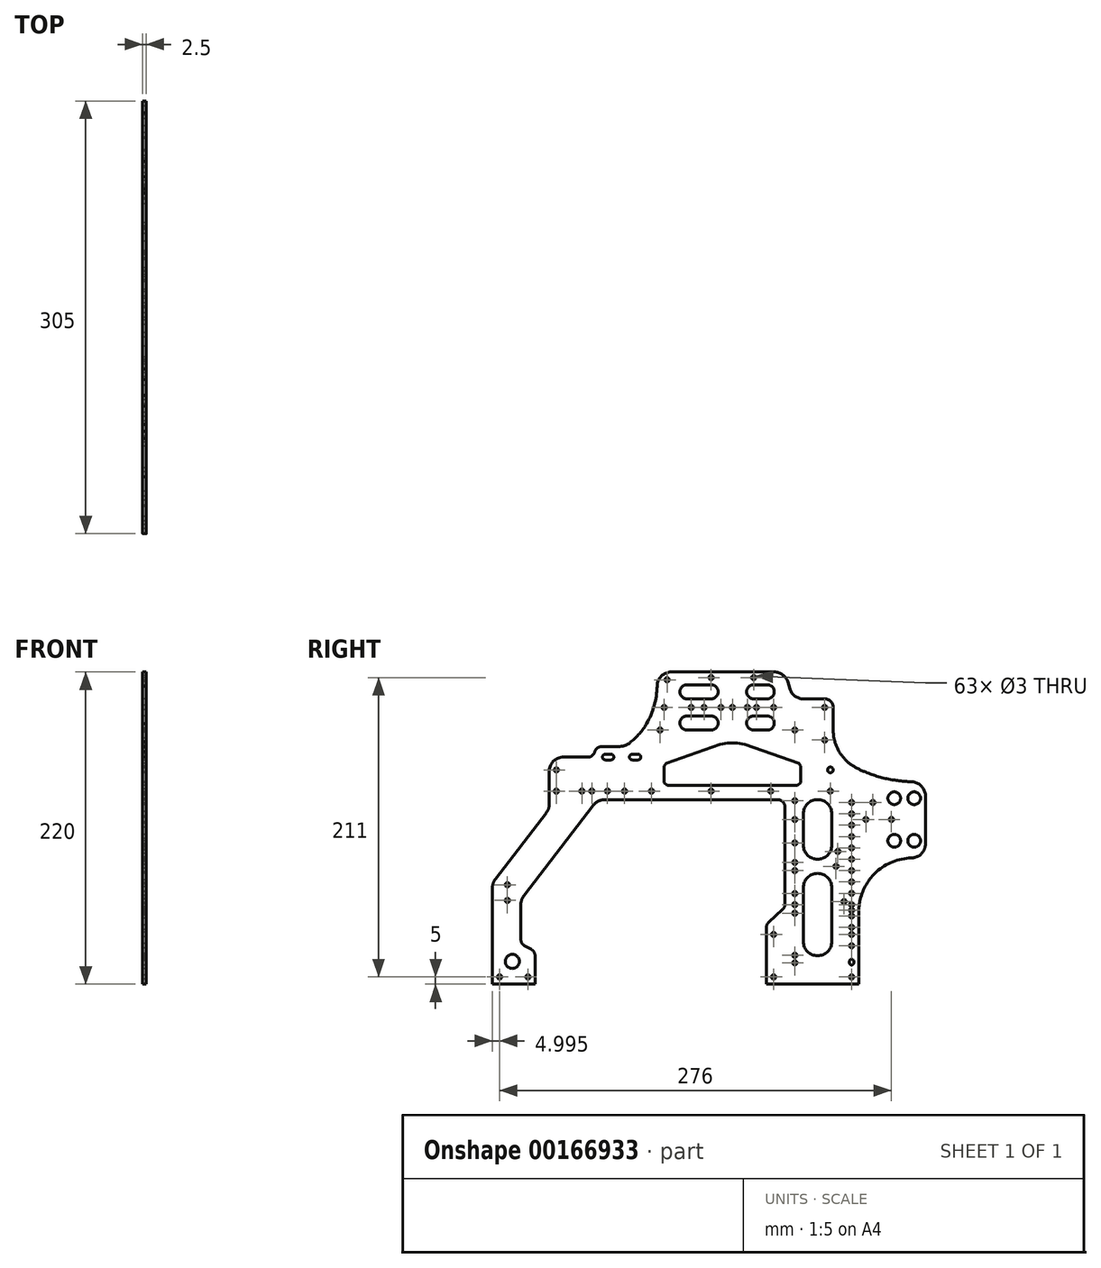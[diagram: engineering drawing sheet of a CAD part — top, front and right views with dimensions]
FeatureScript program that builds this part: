
annotation { "Feature Type Name" : "Feature", "Feature Type Description" : "" }
export const myFeature = defineFeature(function(context is Context, id is Id, definition is map)
    precondition{}
    {
        {
            var Q0;
            Q0=qCreatedBy(makeId("Right.planeOp"),FACE);
            var sketch = newSketch(context, id + "F0", { "sketchPlane" : qUnion([Q0])});
            skLineSegment(sketch, "E0", {"start": v(13.27, 60) * mm, "end": v(19.72, 60) * mm});
            skLineSegment(sketch, "E1", {"start": v(19.72, 60) * mm, "end": v(25.1, 59.07) * mm});
            skLineSegment(sketch, "E2", {"start": v(25.1, 59.07) * mm, "end": v(63.17, 45.47) * mm});
            skLineSegment(sketch, "E3", {"start": v(63.17, 45.47) * mm, "end": v(64.5, 43.6) * mm});
            skLineSegment(sketch, "E4", {"start": v(64.5, 43.6) * mm, "end": v(64.5, 32) * mm});
            skLineSegment(sketch, "E5", {"start": v(64.5, 32) * mm, "end": v(62.5, 30) * mm});
            skLineSegment(sketch, "E6", {"start": v(62.5, 30) * mm, "end": v(-29.5, 30) * mm});
            skLineSegment(sketch, "E7", {"start": v(-29.5, 30) * mm, "end": v(-31.5, 32) * mm});
            skLineSegment(sketch, "E8", {"start": v(-31.5, 32) * mm, "end": v(-31.5, 43.6) * mm});
            skLineSegment(sketch, "E9", {"start": v(-31.5, 43.6) * mm, "end": v(-30.18, 45.47) * mm});
            skLineSegment(sketch, "E10", {"start": v(-30.18, 45.47) * mm, "end": v(7.89, 59.07) * mm});
            skLineSegment(sketch, "E11", {"start": v(7.89, 59.07) * mm, "end": v(13.27, 60) * mm});
            skCircle(sketch, "E12", {"center": v(-138.5, -94) * mm, "radius": 5 * mm});
            skCircle(sketch, "E13", {"center": v(-147.5, -105) * mm, "radius": 1.5 * mm});
            skCircle(sketch, "E14", {"center": v(-127.5, -105) * mm, "radius": 1.5 * mm});
            skCircle(sketch, "E15", {"center": v(-142, -51) * mm, "radius": 1.5 * mm});
            skCircle(sketch, "E16", {"center": v(-142, -40) * mm, "radius": 1.5 * mm});
            skCircle(sketch, "E17", {"center": v(-107.5, 26) * mm, "radius": 1.5 * mm});
            skCircle(sketch, "E18", {"center": v(-107.5, 41) * mm, "radius": 1.5 * mm});
            skCircle(sketch, "E19", {"center": v(-89.5, 26) * mm, "radius": 1.5 * mm});
            skCircle(sketch, "E20", {"center": v(-82.5, 26) * mm, "radius": 1.5 * mm});
            skCircle(sketch, "E21", {"center": v(-71.5, 26) * mm, "radius": 1.5 * mm});
            skArc(sketch, "E22", {"start": v(-75, 50) * mm, "mid": v(-74.42, 48.59) * mm, "end": v(-73, 48) * mm});
            skLineSegment(sketch, "E23", {"start": v(-73, 48) * mm, "end": v(-69, 48) * mm});
            skArc(sketch, "E24", {"start": v(-69, 48) * mm, "mid": v(-67.6, 48.59) * mm, "end": v(-67, 50) * mm});
            skArc(sketch, "E25", {"start": v(-67, 50) * mm, "mid": v(-67.6, 51.41) * mm, "end": v(-69, 52) * mm});
            skLineSegment(sketch, "E26", {"start": v(-69, 52) * mm, "end": v(-73, 52) * mm});
            skArc(sketch, "E27", {"start": v(-73, 52) * mm, "mid": v(-74.42, 51.41) * mm, "end": v(-75, 50) * mm});
            skArc(sketch, "E28", {"start": v(-56, 50) * mm, "mid": v(-55.42, 48.59) * mm, "end": v(-54, 48) * mm});
            skLineSegment(sketch, "E29", {"start": v(-54, 48) * mm, "end": v(-50, 48) * mm});
            skArc(sketch, "E30", {"start": v(-50, 48) * mm, "mid": v(-48.6, 48.59) * mm, "end": v(-48, 50) * mm});
            skArc(sketch, "E31", {"start": v(-48, 50) * mm, "mid": v(-48.6, 51.41) * mm, "end": v(-50, 52) * mm});
            skLineSegment(sketch, "E32", {"start": v(-50, 52) * mm, "end": v(-54, 52) * mm});
            skArc(sketch, "E33", {"start": v(-54, 52) * mm, "mid": v(-55.42, 51.41) * mm, "end": v(-56, 50) * mm});
            skCircle(sketch, "E34", {"center": v(-40.5, 26) * mm, "radius": 1.5 * mm});
            skCircle(sketch, "E35", {"center": v(1.5, 26) * mm, "radius": 1.5 * mm});
            skCircle(sketch, "E36", {"center": v(43.5, 26) * mm, "radius": 1.5 * mm});
            skCircle(sketch, "E37", {"center": v(60.5, 6) * mm, "radius": 1.5 * mm});
            skCircle(sketch, "E38", {"center": v(60.5, -10.5) * mm, "radius": 1.5 * mm});
            skLineSegment(sketch, "E39", {"start": v(66.5, 10) * mm, "end": v(66.5, -12) * mm});
            skArc(sketch, "E40", {"start": v(66.5, -12) * mm, "mid": v(69.42, -19.07) * mm, "end": v(76.5, -22) * mm});
            skArc(sketch, "E41", {"start": v(76.5, -22) * mm, "mid": v(83.57, -19.07) * mm, "end": v(86.5, -12) * mm});
            skLineSegment(sketch, "E42", {"start": v(86.5, -12) * mm, "end": v(86.5, 10) * mm});
            skArc(sketch, "E43", {"start": v(86.5, 10) * mm, "mid": v(83.57, 17.07) * mm, "end": v(76.5, 20) * mm});
            skArc(sketch, "E44", {"start": v(76.5, 20) * mm, "mid": v(69.42, 17.07) * mm, "end": v(66.5, 10) * mm});
            skLineSegment(sketch, "E45", {"start": v(66.5, -42) * mm, "end": v(66.5, -80) * mm});
            skArc(sketch, "E46", {"start": v(66.5, -80) * mm, "mid": v(69.42, -87.07) * mm, "end": v(76.5, -90) * mm});
            skArc(sketch, "E47", {"start": v(76.5, -90) * mm, "mid": v(83.57, -87.07) * mm, "end": v(86.5, -80) * mm});
            skLineSegment(sketch, "E48", {"start": v(86.5, -80) * mm, "end": v(86.5, -42) * mm});
            skArc(sketch, "E49", {"start": v(86.5, -42) * mm, "mid": v(83.57, -34.93) * mm, "end": v(76.5, -32) * mm});
            skArc(sketch, "E50", {"start": v(76.5, -32) * mm, "mid": v(69.42, -34.93) * mm, "end": v(66.5, -42) * mm});
            skCircle(sketch, "E51", {"center": v(130.5, -9) * mm, "radius": 4.5 * mm});
            skCircle(sketch, "E52", {"center": v(144.5, -9) * mm, "radius": 4.5 * mm});
            skCircle(sketch, "E53", {"center": v(130.5, 21) * mm, "radius": 4.5 * mm});
            skCircle(sketch, "E54", {"center": v(144.5, 21) * mm, "radius": 4.5 * mm});
            skArc(sketch, "E55", {"start": v(-20.5, 74) * mm, "mid": v(-19.04, 70.46) * mm, "end": v(-15.5, 69) * mm});
            skLineSegment(sketch, "E56", {"start": v(-15.5, 69) * mm, "end": v(1.5, 69) * mm});
            skArc(sketch, "E57", {"start": v(1.5, 69) * mm, "mid": v(5.03, 70.46) * mm, "end": v(6.5, 74) * mm});
            skArc(sketch, "E58", {"start": v(6.5, 74) * mm, "mid": v(5.03, 77.54) * mm, "end": v(1.5, 79) * mm});
            skLineSegment(sketch, "E59", {"start": v(1.5, 79) * mm, "end": v(-15.5, 79) * mm});
            skArc(sketch, "E60", {"start": v(-15.5, 79) * mm, "mid": v(-19.04, 77.54) * mm, "end": v(-20.5, 74) * mm});
            skArc(sketch, "E61", {"start": v(-20.5, 96) * mm, "mid": v(-19.04, 92.46) * mm, "end": v(-15.5, 91) * mm});
            skLineSegment(sketch, "E62", {"start": v(-15.5, 91) * mm, "end": v(1.5, 91) * mm});
            skArc(sketch, "E63", {"start": v(1.5, 91) * mm, "mid": v(5.03, 92.46) * mm, "end": v(6.5, 96) * mm});
            skArc(sketch, "E64", {"start": v(6.5, 96) * mm, "mid": v(5.03, 99.54) * mm, "end": v(1.5, 101) * mm});
            skLineSegment(sketch, "E65", {"start": v(1.5, 101) * mm, "end": v(-15.5, 101) * mm});
            skArc(sketch, "E66", {"start": v(-15.5, 101) * mm, "mid": v(-19.04, 99.54) * mm, "end": v(-20.5, 96) * mm});
            skArc(sketch, "E67", {"start": v(26.5, 96) * mm, "mid": v(27.96, 92.46) * mm, "end": v(31.5, 91) * mm});
            skLineSegment(sketch, "E68", {"start": v(31.5, 91) * mm, "end": v(41, 91) * mm});
            skArc(sketch, "E69", {"start": v(41, 91) * mm, "mid": v(44.53, 92.46) * mm, "end": v(46, 96) * mm});
            skArc(sketch, "E70", {"start": v(46, 96) * mm, "mid": v(44.53, 99.54) * mm, "end": v(41, 101) * mm});
            skLineSegment(sketch, "E71", {"start": v(41, 101) * mm, "end": v(31.5, 101) * mm});
            skArc(sketch, "E72", {"start": v(31.5, 101) * mm, "mid": v(27.96, 99.54) * mm, "end": v(26.5, 96) * mm});
            skArc(sketch, "E73", {"start": v(26.5, 74) * mm, "mid": v(27.96, 70.46) * mm, "end": v(31.5, 69) * mm});
            skLineSegment(sketch, "E74", {"start": v(31.5, 69) * mm, "end": v(41, 69) * mm});
            skArc(sketch, "E75", {"start": v(41, 69) * mm, "mid": v(44.53, 70.46) * mm, "end": v(46, 74) * mm});
            skArc(sketch, "E76", {"start": v(46, 74) * mm, "mid": v(44.53, 77.54) * mm, "end": v(41, 79) * mm});
            skLineSegment(sketch, "E77", {"start": v(41, 79) * mm, "end": v(31.5, 79) * mm});
            skArc(sketch, "E78", {"start": v(31.5, 79) * mm, "mid": v(27.96, 77.54) * mm, "end": v(26.5, 74) * mm});
            skCircle(sketch, "E79", {"center": v(-34.5, 69) * mm, "radius": 1.5 * mm});
            skCircle(sketch, "E80", {"center": v(-31.5, 85) * mm, "radius": 1.5 * mm});
            skCircle(sketch, "E81", {"center": v(-29.5, 104.5) * mm, "radius": 1.5 * mm});
            skCircle(sketch, "E82", {"center": v(-12.5, 85) * mm, "radius": 1.5 * mm});
            skCircle(sketch, "E83", {"center": v(-3.5, 85) * mm, "radius": 1.5 * mm});
            skCircle(sketch, "E84", {"center": v(8.5, 85) * mm, "radius": 1.5 * mm});
            skCircle(sketch, "E85", {"center": v(16.5, 85) * mm, "radius": 1.5 * mm});
            skCircle(sketch, "E86", {"center": v(27, 85) * mm, "radius": 1.5 * mm});
            skCircle(sketch, "E87", {"center": v(33.5, 85) * mm, "radius": 1.5 * mm});
            skCircle(sketch, "E88", {"center": v(45.5, 85) * mm, "radius": 1.5 * mm});
            skCircle(sketch, "E89", {"center": v(1.5, 106) * mm, "radius": 1.5 * mm});
            skCircle(sketch, "E90", {"center": v(31.5, 106) * mm, "radius": 1.5 * mm});
            skCircle(sketch, "E91", {"center": v(81.5, 85) * mm, "radius": 1.5 * mm});
            skCircle(sketch, "E92", {"center": v(60.5, 69) * mm, "radius": 1.5 * mm});
            skCircle(sketch, "E93", {"center": v(60.5, -24.25) * mm, "radius": 1.5 * mm});
            skCircle(sketch, "E94", {"center": v(60.5, -30) * mm, "radius": 1.5 * mm});
            skCircle(sketch, "E95", {"center": v(60.5, 19.25) * mm, "radius": 1.5 * mm});
            skCircle(sketch, "E96", {"center": v(60.5, -46.25) * mm, "radius": 1.5 * mm});
            skCircle(sketch, "E97", {"center": v(60.5, -54) * mm, "radius": 1.5 * mm});
            skCircle(sketch, "E98", {"center": v(60.5, -60) * mm, "radius": 1.5 * mm});
            skCircle(sketch, "E99", {"center": v(45.5, -75) * mm, "radius": 1.5 * mm});
            skCircle(sketch, "E100", {"center": v(45.5, -105) * mm, "radius": 1.5 * mm});
            skCircle(sketch, "E101", {"center": v(60.5, -89.75) * mm, "radius": 1.5 * mm});
            skCircle(sketch, "E102", {"center": v(60.5, -95) * mm, "radius": 1.5 * mm});
            skCircle(sketch, "E103", {"center": v(100.5, -105) * mm, "radius": 1.5 * mm});
            skCircle(sketch, "E104", {"center": v(85.5, 26) * mm, "radius": 1.5 * mm});
            skCircle(sketch, "E105", {"center": v(85.5, 41) * mm, "radius": 2 * mm});
            skCircle(sketch, "E106", {"center": v(100.5, 18) * mm, "radius": 1.5 * mm});
            skCircle(sketch, "E107", {"center": v(100.5, 10) * mm, "radius": 1.5 * mm});
            skCircle(sketch, "E108", {"center": v(100.5, 2) * mm, "radius": 1.5 * mm});
            skCircle(sketch, "E109", {"center": v(110.5, 6) * mm, "radius": 1.5 * mm});
            skCircle(sketch, "E110", {"center": v(115.5, 18) * mm, "radius": 1.5 * mm});
            skCircle(sketch, "E111", {"center": v(128.5, 6) * mm, "radius": 1.5 * mm});
            skCircle(sketch, "E112", {"center": v(100.5, -6) * mm, "radius": 1.5 * mm});
            skCircle(sketch, "E113", {"center": v(100.5, -14) * mm, "radius": 1.5 * mm});
            skCircle(sketch, "E114", {"center": v(90.75, -16.5) * mm, "radius": 1.5 * mm});
            skCircle(sketch, "E115", {"center": v(89.5, -27) * mm, "radius": 1.5 * mm});
            skCircle(sketch, "E116", {"center": v(100.5, -22) * mm, "radius": 1.5 * mm});
            skCircle(sketch, "E117", {"center": v(100.5, -30) * mm, "radius": 1.5 * mm});
            skCircle(sketch, "E118", {"center": v(100.5, -38) * mm, "radius": 1.5 * mm});
            skCircle(sketch, "E119", {"center": v(100.5, -54) * mm, "radius": 1.5 * mm});
            skCircle(sketch, "E120", {"center": v(95.12, -51.87) * mm, "radius": 1.5 * mm});
            skCircle(sketch, "E121", {"center": v(100.5, -46) * mm, "radius": 1.5 * mm});
            skCircle(sketch, "E122", {"center": v(100.5, -58) * mm, "radius": 1.5 * mm});
            skCircle(sketch, "E123", {"center": v(100.5, -62) * mm, "radius": 1.5 * mm});
            skCircle(sketch, "E124", {"center": v(100.5, -70) * mm, "radius": 1.5 * mm});
            skCircle(sketch, "E125", {"center": v(100.5, -75) * mm, "radius": 1.5 * mm});
            skCircle(sketch, "E126", {"center": v(100.5, -83) * mm, "radius": 1.5 * mm});
            skLineSegment(sketch, "E127", {"start": v(99, -94) * mm, "end": v(99, -95) * mm});
            skArc(sketch, "E128", {"start": v(99, -95) * mm, "mid": v(99.43, -96.06) * mm, "end": v(100.5, -96.5) * mm});
            skArc(sketch, "E129", {"start": v(100.5, -96.5) * mm, "mid": v(101.56, -96.06) * mm, "end": v(102, -95) * mm});
            skLineSegment(sketch, "E130", {"start": v(102, -95) * mm, "end": v(102, -94) * mm});
            skArc(sketch, "E131", {"start": v(102, -94) * mm, "mid": v(101.56, -92.94) * mm, "end": v(100.5, -92.5) * mm});
            skArc(sketch, "E132", {"start": v(100.5, -92.5) * mm, "mid": v(99.43, -92.94) * mm, "end": v(99, -94) * mm});
            skLineSegment(sketch, "E133", {"start": v(105.5, -58) * mm, "end": v(105.5, -110) * mm});
            skLineSegment(sketch, "E134", {"start": v(105.5, -110) * mm, "end": v(40.5, -110) * mm});
            skLineSegment(sketch, "E135", {"start": v(40.5, -110) * mm, "end": v(40.5, -70.03) * mm});
            skArc(sketch, "E136", {"start": v(40.5, -70.03) * mm, "mid": v(40.92, -68.02) * mm, "end": v(42.11, -66.35) * mm});
            skLineSegment(sketch, "E137", {"start": v(42.11, -66.35) * mm, "end": v(51.88, -57.39) * mm});
            skArc(sketch, "E138", {"start": v(51.88, -57.39) * mm, "mid": v(53.07, -55.71) * mm, "end": v(53.5, -53.7) * mm});
            skLineSegment(sketch, "E139", {"start": v(53.5, -53.7) * mm, "end": v(53.5, 15) * mm});
            skArc(sketch, "E140", {"start": v(53.5, 15) * mm, "mid": v(52.03, 18.54) * mm, "end": v(48.5, 20) * mm});
            skLineSegment(sketch, "E141", {"start": v(48.5, 20) * mm, "end": v(-73.57, 20) * mm});
            skArc(sketch, "E142", {"start": v(-73.57, 20) * mm, "mid": v(-78, 18.97) * mm, "end": v(-81.5, 16.08) * mm});
            skLineSegment(sketch, "E143", {"start": v(-81.5, 16.08) * mm, "end": v(-130.44, -47.8) * mm});
            skArc(sketch, "E144", {"start": v(-130.44, -47.8) * mm, "mid": v(-131.98, -50.68) * mm, "end": v(-132.5, -53.89) * mm});
            skLineSegment(sketch, "E145", {"start": v(-132.5, -53.89) * mm, "end": v(-132.5, -78.54) * mm});
            skArc(sketch, "E146", {"start": v(-132.5, -78.54) * mm, "mid": v(-131.8, -81.09) * mm, "end": v(-129.91, -82.92) * mm});
            skLineSegment(sketch, "E147", {"start": v(-129.91, -82.92) * mm, "end": v(-125.1, -85.58) * mm});
            skArc(sketch, "E148", {"start": v(-125.1, -85.58) * mm, "mid": v(-123.2, -87.41) * mm, "end": v(-122.5, -89.96) * mm});
            skLineSegment(sketch, "E149", {"start": v(-122.5, -89.96) * mm, "end": v(-122.5, -110) * mm});
            skLineSegment(sketch, "E150", {"start": v(-122.5, -110) * mm, "end": v(-152.5, -110) * mm});
            skLineSegment(sketch, "E151", {"start": v(-152.5, -110) * mm, "end": v(-152.5, -42.06) * mm});
            skArc(sketch, "E152", {"start": v(-152.5, -42.06) * mm, "mid": v(-151.97, -38.85) * mm, "end": v(-150.44, -35.97) * mm});
            skLineSegment(sketch, "E153", {"start": v(-150.44, -35.97) * mm, "end": v(-114.57, 10.8) * mm});
            skArc(sketch, "E154", {"start": v(-114.57, 10.8) * mm, "mid": v(-113.03, 13.68) * mm, "end": v(-112.5, 16.9) * mm});
            skLineSegment(sketch, "E155", {"start": v(-112.5, 16.9) * mm, "end": v(-112.5, 40) * mm});
            skArc(sketch, "E156", {"start": v(-112.5, 40) * mm, "mid": v(-109.58, 47.07) * mm, "end": v(-102.5, 50) * mm});
            skLineSegment(sketch, "E157", {"start": v(-102.5, 50) * mm, "end": v(-85.5, 50) * mm});
            skArc(sketch, "E158", {"start": v(-85.5, 50) * mm, "mid": v(-82.31, 50.95) * mm, "end": v(-80.5, 53.75) * mm});
            skArc(sketch, "E159", {"start": v(-80.5, 53.75) * mm, "mid": v(-78.6, 56.43) * mm, "end": v(-75.5, 57.5) * mm});
            skLineSegment(sketch, "E160", {"start": v(-75.5, 57.5) * mm, "end": v(-62.5, 57.5) * mm});
            skArc(sketch, "E161", {"start": v(-62.5, 57.5) * mm, "mid": v(-58.45, 58.42) * mm, "end": v(-55, 60.75) * mm});
            skArc(sketch, "E162", {"start": v(-55, 60.75) * mm, "mid": v(-48.87, 66.57) * mm, "end": v(-44, 73.5) * mm});
            skArc(sketch, "E163", {"start": v(-44, 73.5) * mm, "mid": v(-38.59, 86.28) * mm, "end": v(-36.5, 100) * mm});
            skArc(sketch, "E164", {"start": v(-36.5, 100) * mm, "mid": v(-33.58, 107.07) * mm, "end": v(-26.5, 110) * mm});
            skLineSegment(sketch, "E165", {"start": v(-26.5, 110) * mm, "end": v(-2, 110) * mm});
            skLineSegment(sketch, "E166", {"start": v(-2, 110) * mm, "end": v(45.98, 110) * mm});
            skArc(sketch, "E167", {"start": v(45.98, 110) * mm, "mid": v(51.99, 108) * mm, "end": v(55.59, 102.78) * mm});
            skLineSegment(sketch, "E168", {"start": v(55.59, 102.78) * mm, "end": v(56.9, 98.22) * mm});
            skArc(sketch, "E169", {"start": v(56.9, 98.22) * mm, "mid": v(60.5, 93) * mm, "end": v(66.51, 91) * mm});
            skLineSegment(sketch, "E170", {"start": v(66.51, 91) * mm, "end": v(72.5, 91) * mm});
            skLineSegment(sketch, "E171", {"start": v(72.5, 91) * mm, "end": v(81.5, 91) * mm});
            skArc(sketch, "E172", {"start": v(81.5, 91) * mm, "mid": v(85.74, 89.24) * mm, "end": v(87.5, 85) * mm});
            skLineSegment(sketch, "E173", {"start": v(87.5, 85) * mm, "end": v(87.5, 68) * mm});
            skArc(sketch, "E174", {"start": v(87.5, 68) * mm, "mid": v(88.4, 61.85) * mm, "end": v(90.5, 56) * mm});
            skArc(sketch, "E175", {"start": v(90.5, 56) * mm, "mid": v(94.17, 50.28) * mm, "end": v(99, 45.5) * mm});
            skArc(sketch, "E176", {"start": v(99, 45.5) * mm, "mid": v(104.4, 42.07) * mm, "end": v(110.25, 39.5) * mm});
            skArc(sketch, "E177", {"start": v(110.25, 39.5) * mm, "mid": v(119.46, 36.21) * mm, "end": v(129, 34) * mm});
            skArc(sketch, "E178", {"start": v(129, 34) * mm, "mid": v(136.47, 33) * mm, "end": v(144, 32.5) * mm});
            skArc(sketch, "E179", {"start": v(144, 32.5) * mm, "mid": v(149.9, 29.23) * mm, "end": v(152.5, 23) * mm});
            skLineSegment(sketch, "E180", {"start": v(152.5, 23) * mm, "end": v(152.5, -10.75) * mm});
            skArc(sketch, "E181", {"start": v(152.5, -10.75) * mm, "mid": v(149.71, -18.04) * mm, "end": v(142.5, -21) * mm});
            skArc(sketch, "E182", {"start": v(142.5, -21) * mm, "mid": v(129.43, -23.82) * mm, "end": v(118, -30.75) * mm});
            skArc(sketch, "E183", {"start": v(118, -30.75) * mm, "mid": v(110.83, -39.67) * mm, "end": v(106.5, -50.25) * mm});
            skArc(sketch, "E184", {"start": v(106.5, -50.25) * mm, "mid": v(105.82, -54.1) * mm, "end": v(105.5, -58) * mm});
            skCircle(sketch, "E185", {"center": v(81.5, 62) * mm, "radius": 1.5 * mm});
            skCircle(sketch, "E186", {"center": v(-59.5, 26) * mm, "radius": 1.5 * mm});
            skSolve(sketch);
        }
        {
            var Q0;
            Q0=makeQuery(id+"F0.imprint","IMPRINT",FACE,{"disambiguationData":[TD([[makeQuery(id+"F0.imprint","IMPRINT",EDGE,{"derivedFrom":sQuery(id+"F0.wireOp",EDGE,"E0")}),1.0]])]});
            extrude(context, id + "F1", {"entities" : qUnion([Q0]), "endBound" : BoundingType.SYMMETRIC, "depth" : 2.5 * mm});
        }
    });
